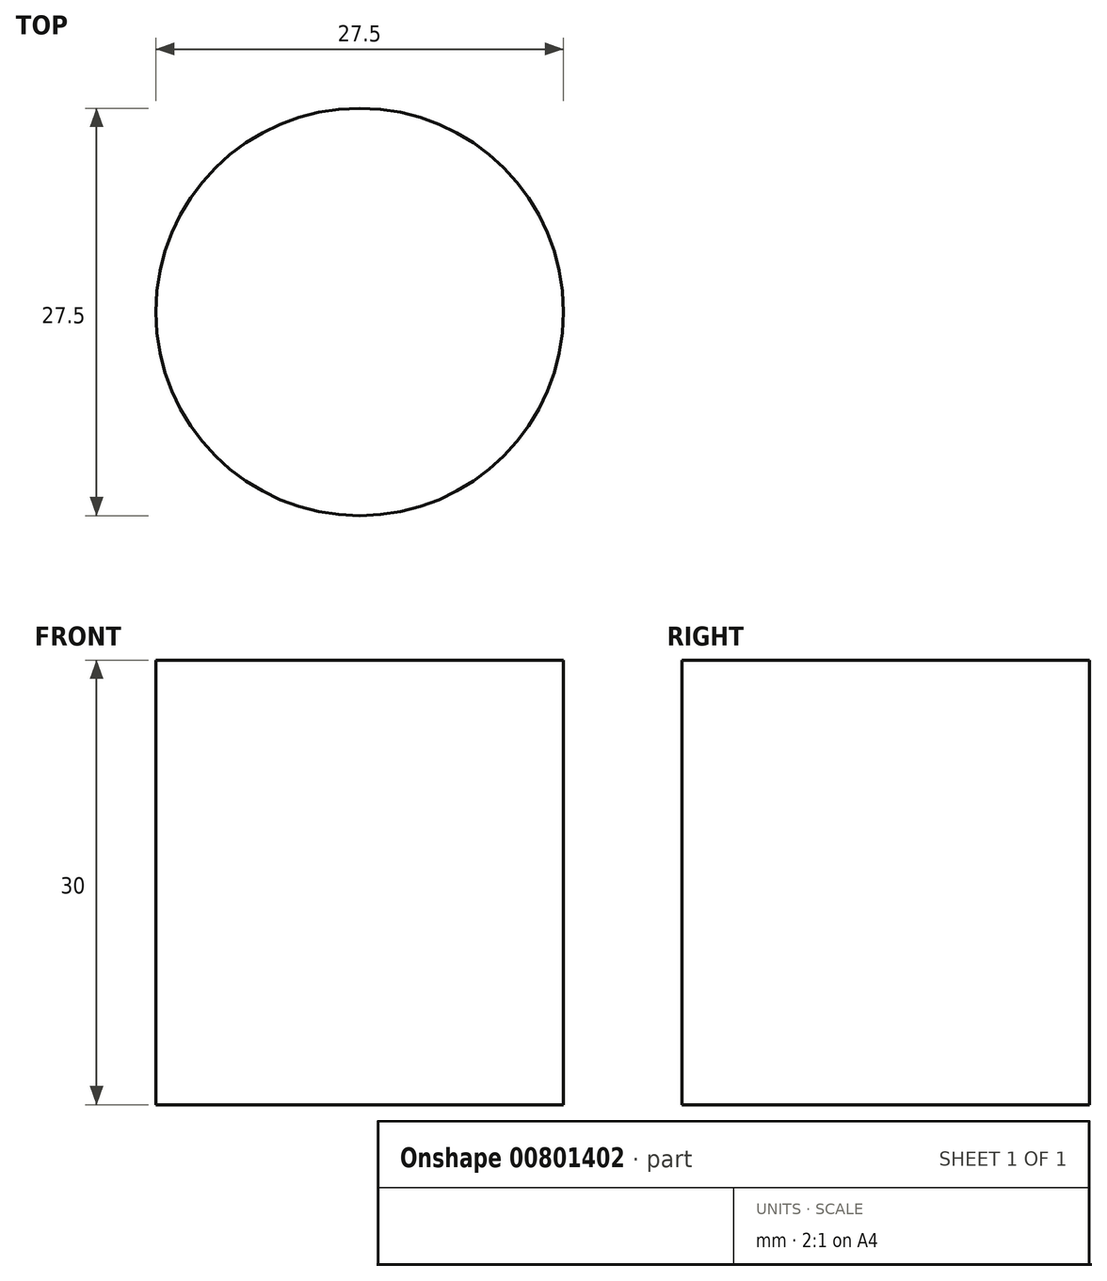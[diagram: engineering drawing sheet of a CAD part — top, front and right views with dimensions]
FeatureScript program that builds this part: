
annotation { "Feature Type Name" : "Feature", "Feature Type Description" : "" }
export const myFeature = defineFeature(function(context is Context, id is Id, definition is map)
    precondition{}
    {
        {
            var Q0;
            Q0=qCreatedBy(makeId("Front.planeOp"),FACE);
            var sketch = newSketch(context, id + "F0", { "sketchPlane" : qUnion([Q0])});
            skLineSegment(sketch, "E0", {"start": v(0, 0) * mm, "end": v(-13.75, 0) * mm});
            skLineSegment(sketch, "E1", {"start": v(-13.75, 0) * mm, "end": v(-13.75, 30) * mm});
            skLineSegment(sketch, "E2", {"start": v(-13.75, 30) * mm, "end": v(0, 30) * mm});
            skLineSegment(sketch, "E3", {"start": v(0, 30) * mm, "end": v(0, 0) * mm});
            skSolve(sketch);
        }
        {
            var Q0;
            Q0 = qSketchRegion(id + "F0", true);
            var Q1;
            Q1=sQuery(id+"F0.wireOp",EDGE,"E3");
            revolve(context, id + "F1", {"surfaceOperationType" : NewSurfaceOperationType.NEW, "entities" : qUnion([Q0]), "axis" : qUnion([Q1]), "revolveType" : RevolveType.FULL});
        }
    });
